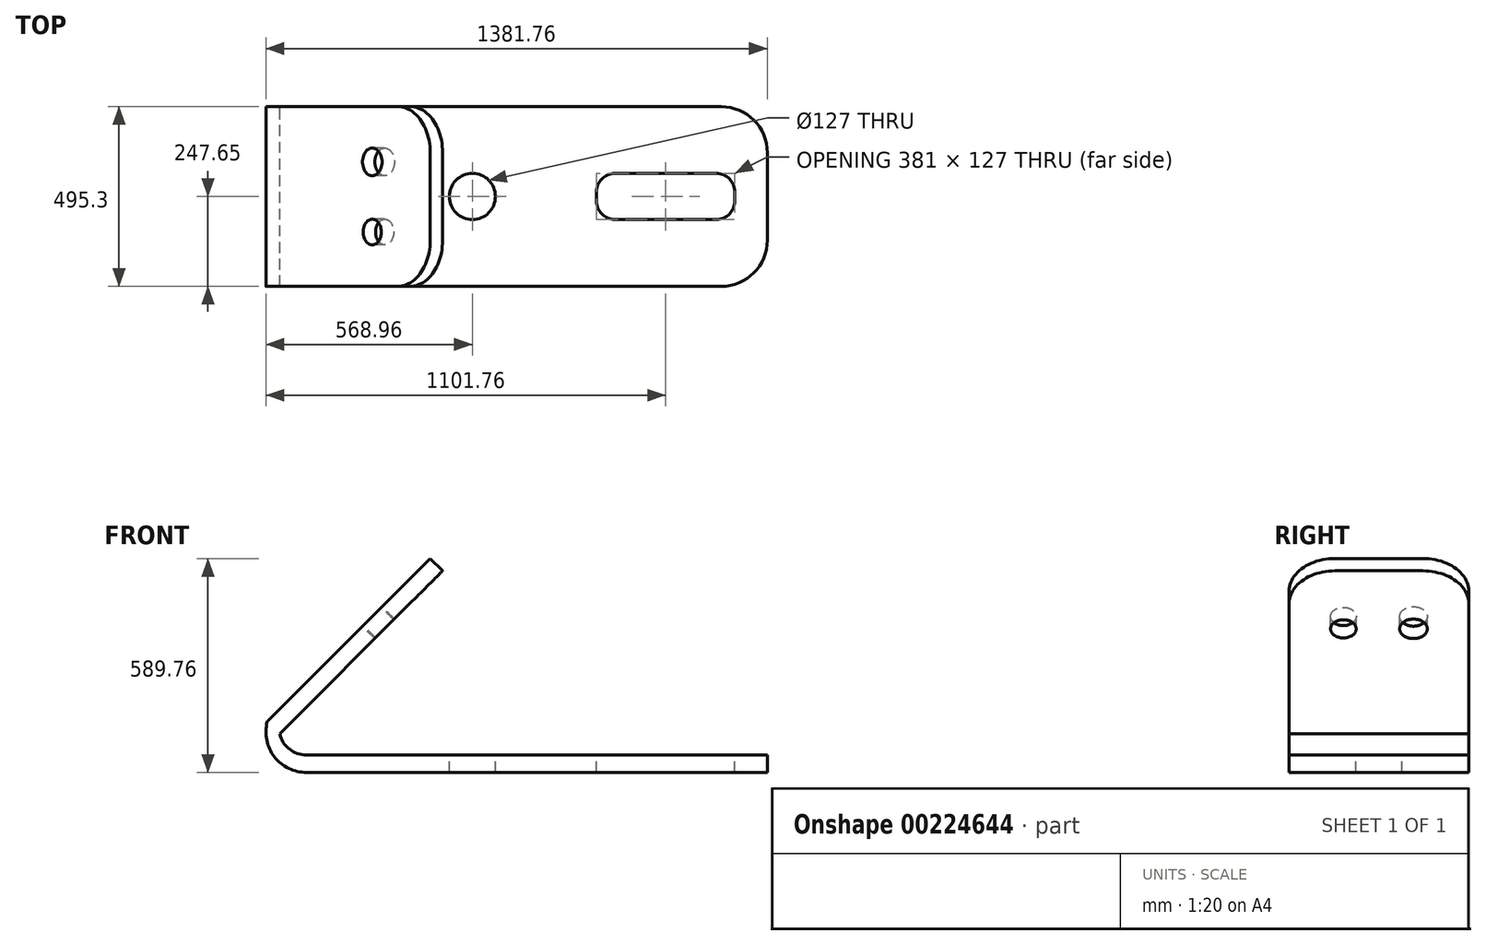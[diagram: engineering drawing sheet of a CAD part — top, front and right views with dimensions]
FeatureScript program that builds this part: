
annotation { "Feature Type Name" : "Feature", "Feature Type Description" : "" }
export const myFeature = defineFeature(function(context is Context, id is Id, definition is map)
    precondition{}
    {
        {
            var Q0;
            Q0=qCreatedBy(makeId("Front.planeOp"),FACE);
            var sketch = newSketch(context, id + "F0", { "sketchPlane" : qUnion([Q0])});
            skLineSegment(sketch, "E0", {"start": v(0, 0) * mm, "end": v(-1270, 0) * mm});
            skLineSegment(sketch, "E1", {"start": v(0, 0) * mm, "end": v(0, 48.26) * mm});
            skLineSegment(sketch, "E2", {"start": v(0, 48.26) * mm, "end": v(-1270, 48.26) * mm});
            skLineSegment(sketch, "E3", {"start": v(-1377.93, 140.75) * mm, "end": v(-928.92, 589.76) * mm});
            skLineSegment(sketch, "E4", {"start": v(-928.92, 589.76) * mm, "end": v(-894.8, 555.64) * mm});
            skLineSegment(sketch, "E5", {"start": v(-894.8, 555.64) * mm, "end": v(-1343.8, 106.62) * mm});
            skArc(sketch, "E6", {"start": v(-1377.93, 140.75) * mm, "mid": v(-1358.69, 43.75) * mm, "end": v(-1270, 0) * mm});
            skArc(sketch, "E7", {"start": v(-1343.8, 106.62) * mm, "mid": v(-1317.05, 64.61) * mm, "end": v(-1270, 48.26) * mm});
            skSolve(sketch);
        }
        {
            var Q0;
            Q0=makeQuery(id+"F0.imprint","IMPRINT",FACE,{"disambiguationData":[TD([[makeQuery(id+"F0.imprint","IMPRINT",EDGE,{"derivedFrom":sQuery(id+"F0.wireOp",EDGE,"E0")}),-1.0]])]});
            extrude(context, id + "F1", {"entities" : qUnion([Q0]), "endBound" : BoundingType.SYMMETRIC, "depth" : 495.3 * mm});
        }
        {
            var Q0;
            Q0=makeQuery(id+"F1.opExtrude","SWEPT_EDGE",EDGE,{"disambiguationData":[OSD([sQuery(id+"F0.wireOp",EDGE,"E3"),sQuery(id+"F0.wireOp",EDGE,"E6")])]});
            fillet(context, id + "F2", {"entities" : qUnion([Q0]), "radius" : 5.08 * mm, "tangentPropagation" : true, "allowEdgeOverflow" : false});
        }
        {
            var Q0;
            Q0=makeQuery(id+"F1.opExtrude","SWEPT_FACE",FACE,{"disambiguationData":[OSD([sQuery(id+"F0.wireOp",EDGE,"E3")])]});
            var sketch = newSketch(context, id + "F3", { "sketchPlane" : qUnion([Q0])});
            skCircle(sketch, "E8", {"center": v(-95.25, -465.72) * mm, "radius": 38.1 * mm});
            skCircle(sketch, "E9", {"center": v(97.95, -465.72) * mm, "radius": 35.4 * mm});
            skSolve(sketch);
        }
        {
            var Q0;
            Q0 = qSketchRegion(id + "F3", true);
            extrude(context, id + "F4", {"entities" : qUnion([Q0]), "operationType" : NewBodyOperationType.REMOVE, "oppositeDirection" : true, "depth" : 127 * mm});
        }
        {
            var Q0;
            Q0=makeQuery(id+"F1.opExtrude","CAP_EDGE",EDGE,{"disambiguationData":[OSD([sQuery(id+"F0.wireOp",EDGE,"E1")])],"isStart":false});
            var Q1;
            Q1=makeQuery(id+"F1.opExtrude","CAP_EDGE",EDGE,{"disambiguationData":[OSD([sQuery(id+"F0.wireOp",EDGE,"E1")])],"isStart":true});
            fillet(context, id + "F5", {"entities" : qUnion([Q0, Q1]), "radius" : 127 * mm, "tangentPropagation" : true, "allowEdgeOverflow" : false});
        }
        {
            var Q0;
            Q0=makeQuery(id+"F1.opExtrude","CAP_EDGE",EDGE,{"disambiguationData":[OSD([sQuery(id+"F0.wireOp",EDGE,"E4")])],"isStart":false});
            var Q1;
            Q1=makeQuery(id+"F1.opExtrude","CAP_EDGE",EDGE,{"disambiguationData":[OSD([sQuery(id+"F0.wireOp",EDGE,"E4")])],"isStart":true});
            fillet(context, id + "F6", {"entities" : qUnion([Q0, Q1]), "radius" : 127 * mm, "tangentPropagation" : true, "allowEdgeOverflow" : false});
        }
        {
            var Q0;
            Q0=makeQuery(id+"F1.opExtrude","SWEPT_FACE",FACE,{"disambiguationData":[OSD([sQuery(id+"F0.wireOp",EDGE,"E2")])]});
            var sketch = newSketch(context, id + "F7", { "sketchPlane" : qUnion([Q0])});
            skLineSegment(sketch, "E10", {"start": v(0, 0) * mm, "end": v(-812.8, 0) * mm});
            skCircle(sketch, "E11", {"center": v(-812.8, 0) * mm, "radius": 63.5 * mm});
            skSolve(sketch);
        }
        {
            var Q0;
            Q0 = qSketchRegion(id + "F7", true);
            extrude(context, id + "F8", {"entities" : qUnion([Q0]), "operationType" : NewBodyOperationType.REMOVE, "oppositeDirection" : true, "depth" : 127 * mm});
        }
        {
            var Q0;
            Q0=makeQuery(id+"F1.opExtrude","SWEPT_FACE",FACE,{"disambiguationData":[OSD([sQuery(id+"F0.wireOp",EDGE,"E2")])]});
            var sketch = newSketch(context, id + "F9", { "sketchPlane" : qUnion([Q0])});
            skLineSegment(sketch, "E12.bottom", {"start": v(-89.5, -63.5) * mm, "end": v(-470.5, -63.5) * mm});
            skLineSegment(sketch, "E12.top", {"start": v(-89.5, 63.5) * mm, "end": v(-470.5, 63.5) * mm});
            skLineSegment(sketch, "E12.left", {"start": v(-89.5, -63.5) * mm, "end": v(-89.5, 63.5) * mm});
            skLineSegment(sketch, "E12.right", {"start": v(-470.5, -63.5) * mm, "end": v(-470.5, 63.5) * mm});
            skPoint(sketch, "E12.middle", {"position": v(-280, 0) * mm});
            skSolve(sketch);
        }
        {
            var Q0;
            Q0=makeQuery(id+"F9.imprint","IMPRINT",FACE,{"disambiguationData":[TD([[makeQuery(id+"F9.imprint","IMPRINT",EDGE,{"derivedFrom":sQuery(id+"F9.wireOp",EDGE,"E12.bottom")}),-1.0]])]});
            extrude(context, id + "F10", {"entities" : qUnion([Q0]), "operationType" : NewBodyOperationType.REMOVE, "oppositeDirection" : true, "depth" : 127 * mm});
        }
        {
            var Q0;
            Q0=makeQuery(id+"F10.boolean.opBoolean","COPY",EDGE,{"derivedFrom":makeQuery(id+"F10.opExtrude","SWEPT_EDGE",EDGE,{"disambiguationData":[OSD([sQuery(id+"F9.wireOp",EDGE,"E12.top"),sQuery(id+"F9.wireOp",EDGE,"E12.right")])]})});
            var Q1;
            Q1=makeQuery(id+"F10.boolean.opBoolean","COPY",EDGE,{"derivedFrom":makeQuery(id+"F10.opExtrude","SWEPT_EDGE",EDGE,{"disambiguationData":[OSD([sQuery(id+"F9.wireOp",EDGE,"E12.bottom"),sQuery(id+"F9.wireOp",EDGE,"E12.right")])]})});
            var Q2;
            Q2=makeQuery(id+"F10.boolean.opBoolean","COPY",EDGE,{"derivedFrom":makeQuery(id+"F10.opExtrude","SWEPT_EDGE",EDGE,{"disambiguationData":[OSD([sQuery(id+"F9.wireOp",EDGE,"E12.top"),sQuery(id+"F9.wireOp",EDGE,"E12.left")])]})});
            var Q3;
            Q3=makeQuery(id+"F10.boolean.opBoolean","COPY",EDGE,{"derivedFrom":makeQuery(id+"F10.opExtrude","SWEPT_EDGE",EDGE,{"disambiguationData":[OSD([sQuery(id+"F9.wireOp",EDGE,"E12.bottom"),sQuery(id+"F9.wireOp",EDGE,"E12.left")])]})});
            fillet(context, id + "F11", {"entities" : qUnion([Q0, Q1, Q2, Q3]), "radius" : 50.8 * mm, "tangentPropagation" : true, "allowEdgeOverflow" : false});
        }
    });
